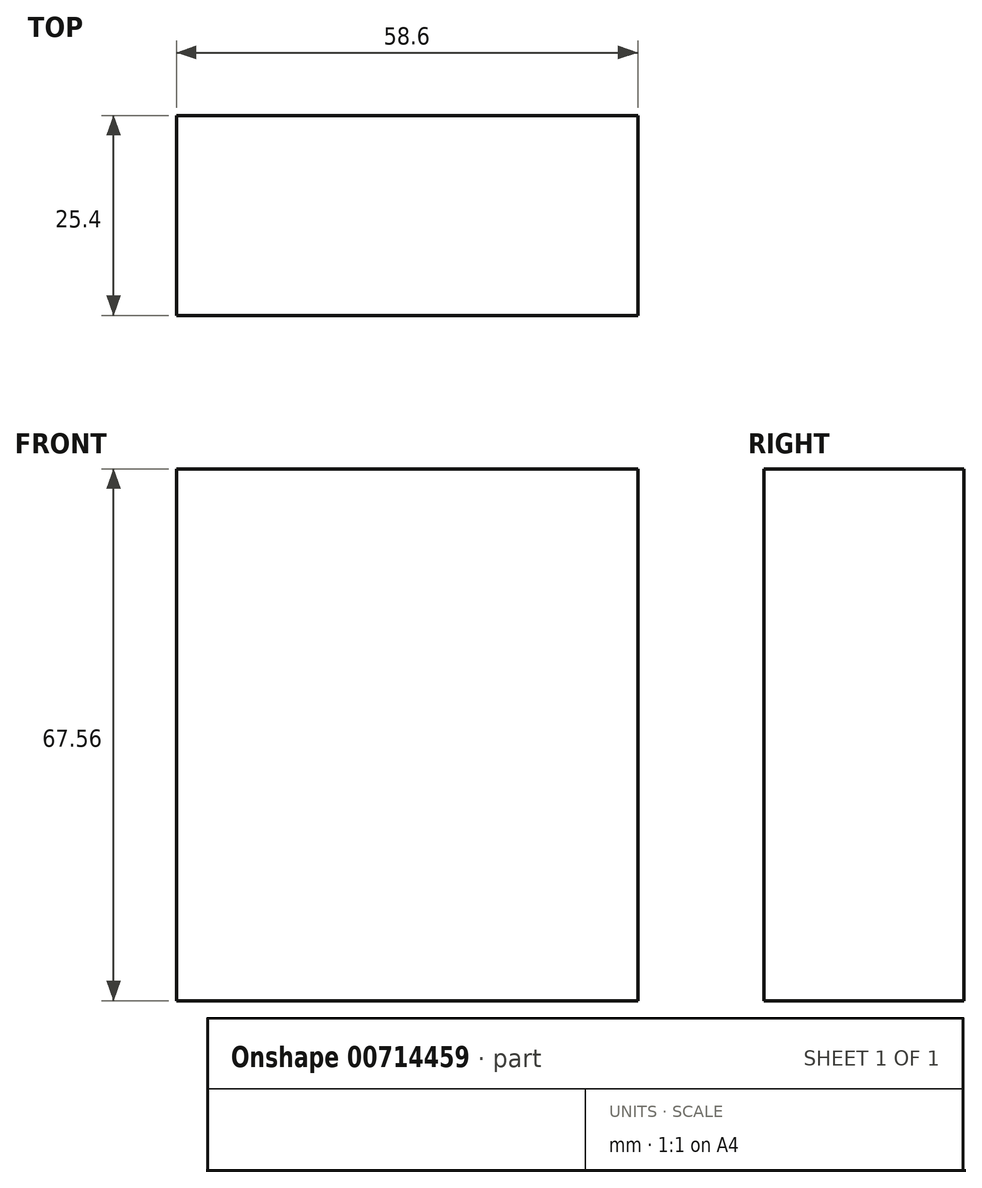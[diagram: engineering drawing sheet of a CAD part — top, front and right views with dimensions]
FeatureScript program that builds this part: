
annotation { "Feature Type Name" : "Feature", "Feature Type Description" : "" }
export const myFeature = defineFeature(function(context is Context, id is Id, definition is map)
    precondition{}
    {
        {
            var Q0;
            Q0=qCreatedBy(makeId("Front.planeOp"),FACE);
            var sketch = newSketch(context, id + "F0", { "sketchPlane" : qUnion([Q0])});
            skLineSegment(sketch, "E0.bottom", {"start": v(-32.69, -37.26) * mm, "end": v(25.91, -37.26) * mm});
            skLineSegment(sketch, "E0.top", {"start": v(-32.69, 30.3) * mm, "end": v(25.91, 30.3) * mm});
            skLineSegment(sketch, "E0.left", {"start": v(-32.69, -37.26) * mm, "end": v(-32.69, 30.3) * mm});
            skLineSegment(sketch, "E0.right", {"start": v(25.91, -37.26) * mm, "end": v(25.91, 30.3) * mm});
            skSolve(sketch);
        }
        {
            var Q0;
            Q0=makeQuery(id+"F0.imprint","IMPRINT",FACE,{"disambiguationData":[TD([[makeQuery(id+"F0.imprint","IMPRINT",EDGE,{"derivedFrom":sQuery(id+"F0.wireOp",EDGE,"E0.bottom")}),1.0]])]});
            extrude(context, id + "F1", {"entities" : qUnion([Q0]), "depth" : 25.4 * mm, "offsetDistance" : 25.4 * mm});
        }
    });
